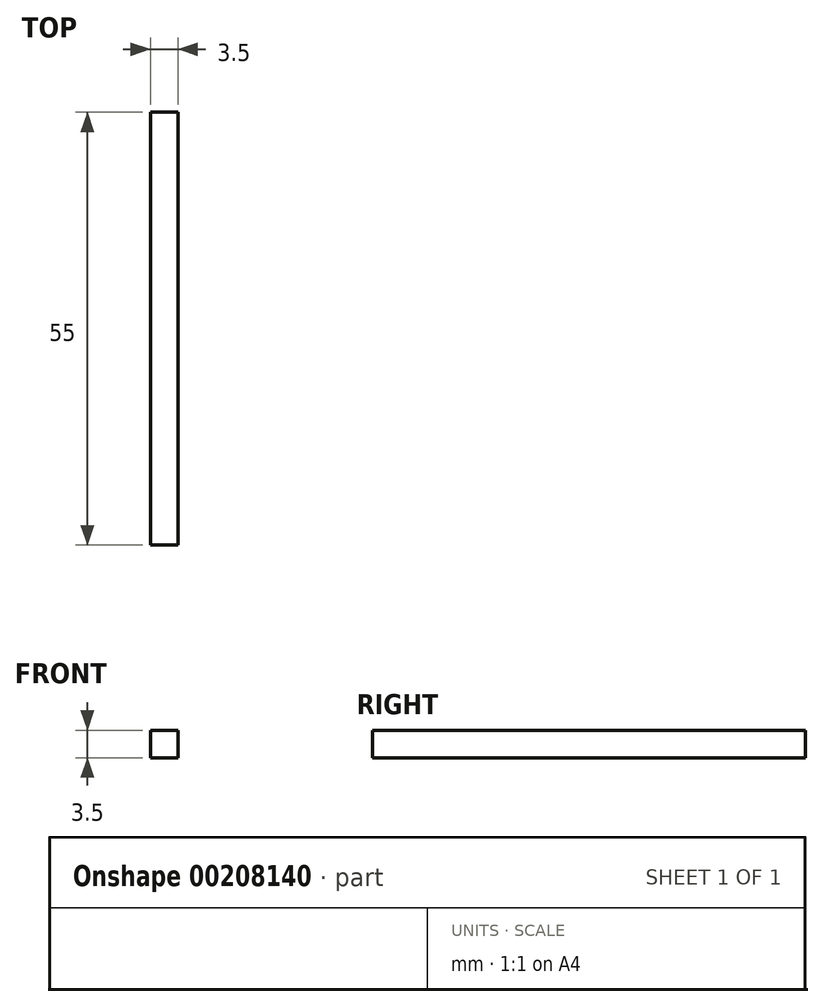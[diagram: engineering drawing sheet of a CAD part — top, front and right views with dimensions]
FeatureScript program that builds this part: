
annotation { "Feature Type Name" : "Feature", "Feature Type Description" : "" }
export const myFeature = defineFeature(function(context is Context, id is Id, definition is map)
    precondition{}
    {
        {
            var Q0;
            Q0=qCreatedBy(makeId("Top.planeOp"),FACE);
            var sketch = newSketch(context, id + "F0", { "sketchPlane" : qUnion([Q0])});
            skLineSegment(sketch, "E0.bottom", {"start": v(1.75, 27.5) * mm, "end": v(-1.75, 27.5) * mm});
            skLineSegment(sketch, "E0.top", {"start": v(1.75, -27.5) * mm, "end": v(-1.75, -27.5) * mm});
            skLineSegment(sketch, "E0.left", {"start": v(1.75, 27.5) * mm, "end": v(1.75, -27.5) * mm});
            skLineSegment(sketch, "E0.right", {"start": v(-1.75, 27.5) * mm, "end": v(-1.75, -27.5) * mm});
            skPoint(sketch, "E0.middle", {"position": v(0, 0) * mm});
            skSolve(sketch);
        }
        {
            var Q0;
            Q0 = qSketchRegion(id + "F0", true);
            extrude(context, id + "F1", {"entities" : qUnion([Q0]), "depth" : 3.5 * mm});
        }
    });
